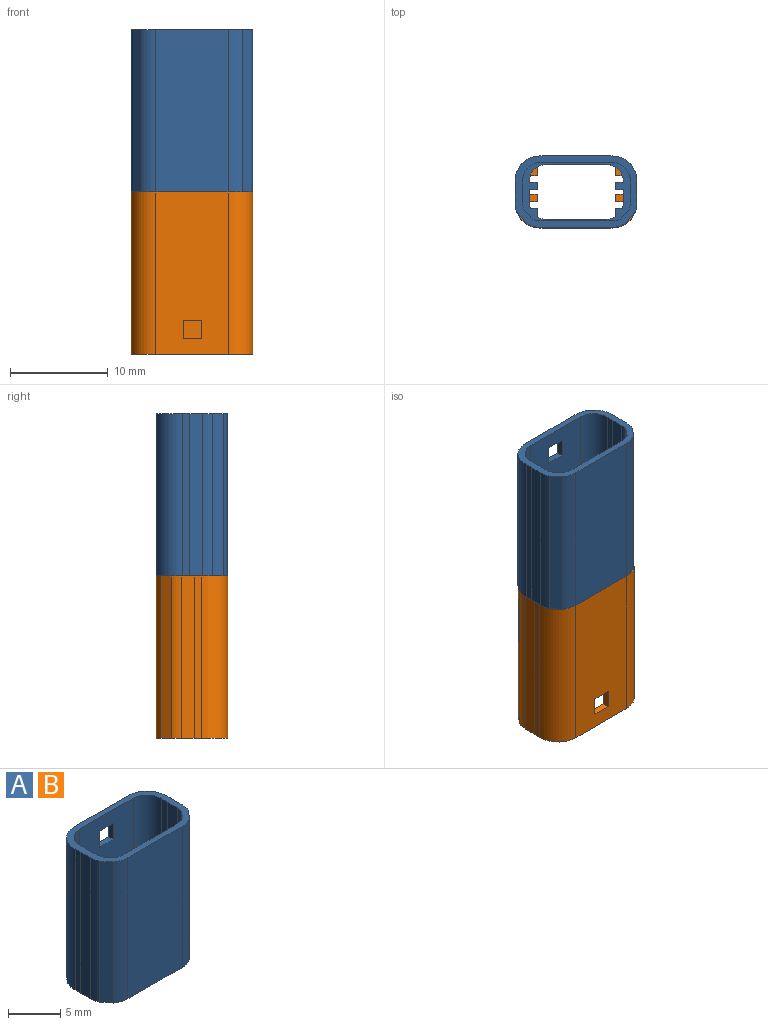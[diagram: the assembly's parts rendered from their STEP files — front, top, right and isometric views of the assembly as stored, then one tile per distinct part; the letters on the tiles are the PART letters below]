
ASSEMBLY  parts=2 mates=1
PART A: 57 faces, bbox 12.5x7.3x16.6 mm
  f0: plane 16.6x0.78mm, normal (1,0,0), area 12.9mm2, adj f1,f12,f33,f56
  f1: plane 16.6x1.3mm, normal (1,0,0), area 21.6mm2, adj f0,f12,f34,f56
  f2: plane 16.6x7.37mm, normal (0,1,0), area 118.7mm2, adj f12,f32,f33,f52,f53,f54,f55,f56
  f3: plane 8.6x7.23mm, normal (0,-1,0), area 58.6mm2, adj f12,f25,f40,f41,f52,f53,f54,f55
  f4: cylinder r=1.7mm len=8mm, axis (0,0,-1), area 22.2mm2, adj f5,f15,f25,f56
  f5: plane 8x6.2mm, normal (0,-1,0), area 49.6mm2, adj f4,f6,f25,f56
  f6: cylinder r=1.7mm len=8mm, axis (0,0,-1), area 22.2mm2, adj f5,f16,f25,f56
  f7: cylinder r=1.7mm len=8mm, axis (0,0,-1), area 4.9mm2, adj f19,f20,f25,f56
  f8: cylinder r=1.7mm len=8mm, axis (0,0,-1), area 7.6mm2, adj f9,f21,f25,f56
  f9: plane 8x6.2mm, normal (0,1,0), area 49.6mm2, adj f8,f10,f25,f56
  f10: cylinder r=1.7mm len=8mm, axis (0,0,-1), area 7.6mm2, adj f9,f22,f25,f56
  f11: cylinder r=1.7mm len=8mm, axis (0,0,-1), area 4.9mm2, adj f23,f24,f25,f56
  f12: plane 12.47x7.3mm, normal (0,0,1), area 22.3mm2, adj f0,f1,f2,f3,f26,f27,f28,f29
  f13: plane 8x0.8mm, normal (0,-1,0), area 6.4mm2, adj f14,f24,f25,f56
  f14: plane 8x0.8mm, normal (1,0,0), area 6.4mm2, adj f13,f15,f25,f56
  f15: plane 8x0.8mm, normal (0,1,0), area 6.4mm2, adj f4,f14,f25,f56
  f16: plane 8x0.8mm, normal (0,1,0), area 6.4mm2, adj f6,f17,f25,f56
  f17: plane 8x0.8mm, normal (-1,0,0), area 6.4mm2, adj f16,f18,f25,f56
  f18: plane 8x0.8mm, normal (0,-1,0), area 6.4mm2, adj f17,f19,f25,f56
  f19: plane 8x1.3mm, normal (-1,0,0), area 10.4mm2, adj f7,f18,f25,f56
  f20: plane 8x0.69mm, normal (0,1,0), area 5.5mm2, adj f7,f21,f25,f56
  f21: plane 8x0.84mm, normal (-1,0,0), area 6.7mm2, adj f8,f20,f25,f56
  f22: plane 8x0.84mm, normal (1,0,0), area 6.7mm2, adj f10,f23,f25,f56
  f23: plane 8x0.69mm, normal (0,1,0), area 5.5mm2, adj f11,f22,f25,f56
  f24: plane 8x1.3mm, normal (1,0,0), area 10.4mm2, adj f11,f13,f25,f56
  f25: plane 11.03x6mm, normal (0,0,1), area 13.7mm2, adj f3,f4,f5,f6,f7,f8,f9,f10
  f26: plane 16.6x7.37mm, normal (0,-1,0), area 122.3mm2, adj f12,f27,f36,f56
  f27: cylinder r=2.55mm len=16.6mm, axis (0,0,-1), area 26.2mm2, adj f12,f26,f28,f56
  f28: plane 16.6x1.04mm, normal (-0.77,-0.63,0), area 22.2mm2, adj f12,f27,f29,f56
  f29: cylinder r=2.55mm len=16.6mm, axis (0,0,-1), area 17.8mm2, adj f12,f28,f30,f56
  f30: plane 16.6x1.3mm, normal (-1,0,0), area 21.6mm2, adj f12,f29,f31,f56
  f31: plane 16.6x0.78mm, normal (-1,0,0), area 12.9mm2, adj f12,f30,f32,f56
  f32: cylinder r=2.55mm len=16.6mm, axis (0,0,-1), area 68.5mm2, adj f2,f12,f31,f56
  f33: cylinder r=2.55mm len=16.6mm, axis (0,0,-1), area 68.5mm2, adj f0,f2,f12,f56
  f34: cylinder r=2.55mm len=16.6mm, axis (0,0,-1), area 17.8mm2, adj f1,f12,f35,f56
  f35: plane 16.6x1.04mm, normal (0.77,-0.63,0), area 22.2mm2, adj f12,f34,f36,f56
  f36: cylinder r=2.55mm len=16.6mm, axis (0,0,-1), area 26.2mm2, adj f12,f26,f35,f56
  f37: cylinder r=1.9mm len=8.6mm, axis (0,0,1), area 6.2mm2, adj f12,f25,f38,f51
  f38: plane 8.6x1.3mm, normal (-1,0,0), area 11.2mm2, adj f12,f25,f37,f39
  f39: plane 8.6x0.79mm, normal (-1,0,0), area 6.8mm2, adj f12,f25,f38,f40
  f40: cylinder r=1.9mm len=8.6mm, axis (0,0,1), area 26.6mm2, adj f3,f12,f25,f39
  f41: cylinder r=1.9mm len=8.6mm, axis (0,0,1), area 26.6mm2, adj f3,f12,f25,f42
  f42: plane 8.6x0.79mm, normal (1,0,0), area 6.8mm2, adj f12,f25,f41,f43
  f43: plane 8.6x1.3mm, normal (1,0,0), area 11.2mm2, adj f12,f25,f42,f44
  f44: cylinder r=1.9mm len=8.6mm, axis (0,0,1), area 6.2mm2, adj f12,f25,f43,f45
  f45: plane 8.6x0.89mm, normal (0.77,0.63,0), area 9.9mm2, adj f12,f25,f44,f46
  f46: cylinder r=1.9mm len=8.6mm, axis (0,0,1), area 9.4mm2, adj f12,f25,f45,f47
  f47: plane 8.6x0.51mm, normal (0,1,0), area 4.4mm2, adj f12,f25,f46,f48
  f48: plane 8.6x6.2mm, normal (0,1,0), area 53.3mm2, adj f12,f25,f47,f49
  f49: plane 8.6x0.52mm, normal (0,1,0), area 4.5mm2, adj f12,f25,f48,f50
  f50: cylinder r=1.9mm len=8.6mm, axis (0,0,1), area 9.4mm2, adj f12,f25,f49,f51
  f51: plane 8.6x0.89mm, normal (-0.77,0.63,0), area 9.9mm2, adj f12,f25,f37,f50
  f52: plane 1.9x0.65mm, normal (0,0,-1), area 1.2mm2, adj f2,f3,f53,f55
  f53: plane 1.9x0.65mm, normal (-1,0,0), area 1.2mm2, adj f2,f3,f52,f54
  f54: plane 1.9x0.65mm, normal (0,0,1), area 1.2mm2, adj f2,f3,f53,f55
  f55: plane 1.9x0.65mm, normal (1,0,0), area 1.2mm2, adj f2,f3,f52,f54
  f56: plane 12.47x7.3mm, normal (0,0,-1), area 36mm2, adj f0,f1,f2,f4,f5,f6,f7,f8
PART B: same geometry as A
PLACE A t=(5.6,23.31,1.74)mm
PLACE B rot(axis=(1,0,0),180deg) t=(5.6,-69.82,17.74)mm
MATE planar B.f56 <-> A.f56  axis (0,0,1) through (-61.14,-23.25,9.74)mm
